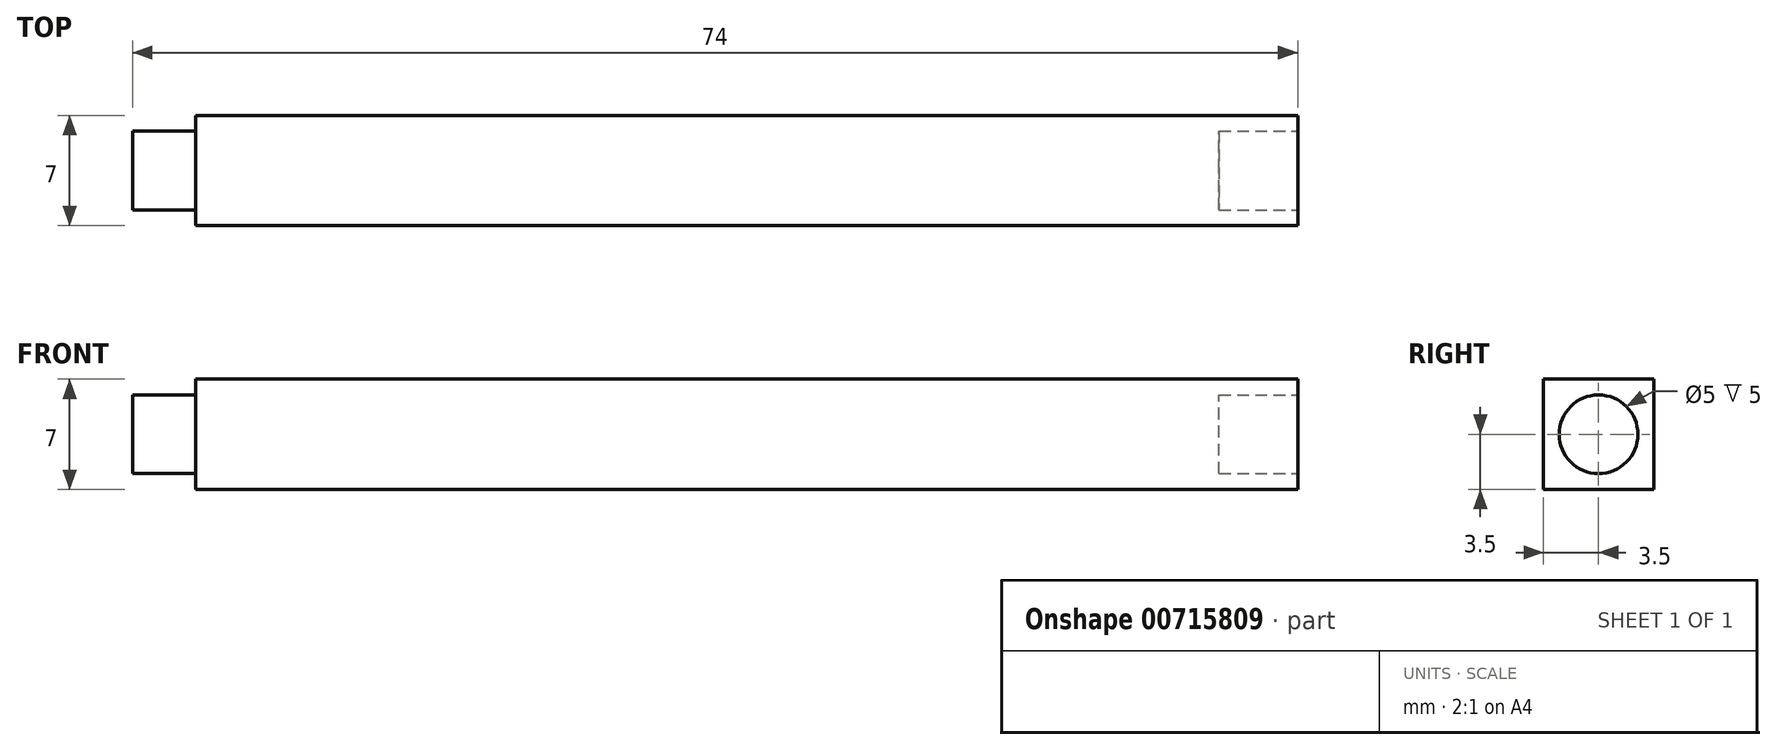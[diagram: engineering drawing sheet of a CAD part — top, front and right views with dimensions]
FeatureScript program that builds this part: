
annotation { "Feature Type Name" : "Feature", "Feature Type Description" : "" }
export const myFeature = defineFeature(function(context is Context, id is Id, definition is map)
    precondition{}
    {
        {
            var Q0;
            Q0=qCreatedBy(makeId("Top.planeOp"),FACE);
            var sketch = newSketch(context, id + "F0", { "sketchPlane" : qUnion([Q0])});
            skLineSegment(sketch, "E0.bottom", {"start": v(0, 0) * mm, "end": v(70, 0) * mm});
            skLineSegment(sketch, "E0.top", {"start": v(0, 7) * mm, "end": v(70, 7) * mm});
            skLineSegment(sketch, "E0.left", {"start": v(0, 0) * mm, "end": v(0, 7) * mm});
            skLineSegment(sketch, "E0.right", {"start": v(70, 0) * mm, "end": v(70, 7) * mm});
            skSolve(sketch);
        }
        {
            var Q0;
            Q0=makeQuery(id+"F0.imprint","IMPRINT",FACE,{"disambiguationData":[TD([[makeQuery(id+"F0.imprint","IMPRINT",EDGE,{"derivedFrom":sQuery(id+"F0.wireOp",EDGE,"E0.bottom")}),1.0]])]});
            extrude(context, id + "F1", {"entities" : qUnion([Q0]), "depth" : 7 * mm, "offsetDistance" : 25 * mm});
        }
        {
            var Q0;
            Q0=makeQuery(id+"F1.opExtrude","SWEPT_FACE",FACE,{"disambiguationData":[OSD([sQuery(id+"F0.wireOp",EDGE,"E0.right")])]});
            var sketch = newSketch(context, id + "F2", { "sketchPlane" : qUnion([Q0])});
            skLineSegment(sketch, "E1", {"start": v(3.5, 7) * mm, "end": v(3.5, 0) * mm, "construction": true});
            skCircle(sketch, "E2", {"center": v(3.5, 3.5) * mm, "radius": 2.5 * mm});
            skSolve(sketch);
        }
        {
            var Q0;
            Q0=makeQuery(id+"F2.imprint","IMPRINT",FACE,{"disambiguationData":[TD([[makeQuery(id+"F2.imprint","IMPRINT",EDGE,{"derivedFrom":sQuery(id+"F2.wireOp",EDGE,"E2")}),1.0]])]});
            extrude(context, id + "F3", {"entities" : qUnion([Q0]), "operationType" : NewBodyOperationType.REMOVE, "oppositeDirection" : true, "depth" : 5 * mm, "offsetDistance" : 25 * mm});
        }
        {
            var Q0;
            Q0=makeQuery(id+"F1.opExtrude","SWEPT_FACE",FACE,{"disambiguationData":[OSD([sQuery(id+"F0.wireOp",EDGE,"E0.left")])]});
            var sketch = newSketch(context, id + "F4", { "sketchPlane" : qUnion([Q0])});
            skLineSegment(sketch, "E3", {"start": v(-3.5, 7) * mm, "end": v(-3.5, 0) * mm, "construction": true});
            skCircle(sketch, "E4", {"center": v(-3.5, 3.5) * mm, "radius": 2.5 * mm});
            skSolve(sketch);
        }
        {
            var Q0;
            Q0=makeQuery(id+"F4.imprint","IMPRINT",FACE,{"disambiguationData":[TD([[makeQuery(id+"F4.imprint","IMPRINT",EDGE,{"derivedFrom":sQuery(id+"F4.wireOp",EDGE,"E4")}),1.0]])]});
            extrude(context, id + "F5", {"entities" : qUnion([Q0]), "operationType" : NewBodyOperationType.ADD, "depth" : 4 * mm, "offsetDistance" : 25 * mm});
        }
    });
